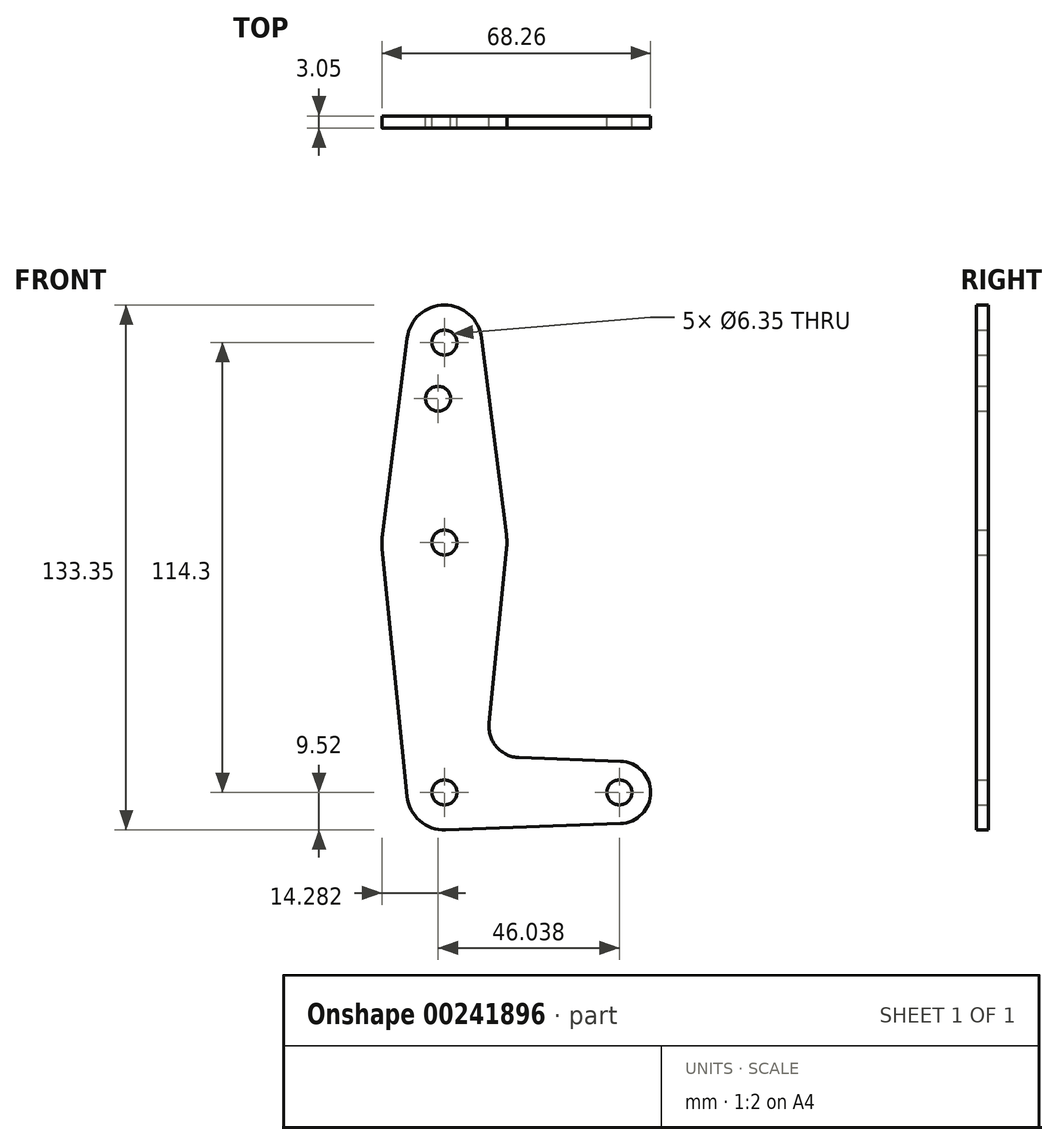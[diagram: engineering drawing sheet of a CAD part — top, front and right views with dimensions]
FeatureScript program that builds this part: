
annotation { "Feature Type Name" : "Feature", "Feature Type Description" : "" }
export const myFeature = defineFeature(function(context is Context, id is Id, definition is map)
    precondition{}
    {
        {
            var Q0;
            Q0=qCreatedBy(makeId("Front.planeOp"),FACE);
            var sketch = newSketch(context, id + "F0", { "sketchPlane" : qUnion([Q0])});
            skCircle(sketch, "E0", {"center": v(0, 0) * mm, "radius": 9.53 * mm});
            skLineSegment(sketch, "E1", {"start": v(0, 0) * mm, "end": v(44.45, 0) * mm, "construction": true});
            skCircle(sketch, "E2", {"center": v(44.45, 0) * mm, "radius": 7.94 * mm});
            skLineSegment(sketch, "E3", {"start": v(0, 0) * mm, "end": v(0, 63.5) * mm, "construction": true});
            skLineSegment(sketch, "E4", {"start": v(0, 63.5) * mm, "end": v(0, 114.3) * mm, "construction": true});
            skCircle(sketch, "E5", {"center": v(0, 63.5) * mm, "radius": 15.88 * mm});
            skCircle(sketch, "E6", {"center": v(0, 114.3) * mm, "radius": 9.53 * mm});
            skLineSegment(sketch, "E7", {"start": v(-9.45, 115.5) * mm, "end": v(-15.75, 65.48) * mm});
            skLineSegment(sketch, "E8", {"start": v(9.45, 115.5) * mm, "end": v(15.75, 65.48) * mm});
            skLineSegment(sketch, "E9", {"start": v(-15.8, 61.91) * mm, "end": v(-9.48, -0.95) * mm});
            skLineSegment(sketch, "E10", {"start": v(15.8, 61.91) * mm, "end": v(11.34, 17.6) * mm});
            skLineSegment(sketch, "E11", {"start": v(18.97, 8.85) * mm, "end": v(44.73, 7.93) * mm});
            skLineSegment(sketch, "E12", {"start": v(0.34, -9.52) * mm, "end": v(44.73, -7.93) * mm});
            skCircle(sketch, "E13", {"center": v(0, 0) * mm, "radius": 3.18 * mm});
            skCircle(sketch, "E14", {"center": v(44.45, 0) * mm, "radius": 3.18 * mm});
            skCircle(sketch, "E15", {"center": v(0, 63.5) * mm, "radius": 3.18 * mm});
            skCircle(sketch, "E16", {"center": v(-1.59, 100.03) * mm, "radius": 3.18 * mm});
            skArc(sketch, "E17.filletArc", {"start": v(11.34, 17.6) * mm, "mid": v(13.26, 11.57) * mm, "end": v(18.97, 8.85) * mm});
            skCircle(sketch, "E18", {"center": v(0, 114.3) * mm, "radius": 3.18 * mm});
            skSolve(sketch);
        }
        {
            var Q0;
            Q0 = qSketchRegion(id + "F0", true);
            extrude(context, id + "F1", {"entities" : qUnion([Q0]), "depth" : 3.05 * mm});
        }
    });
